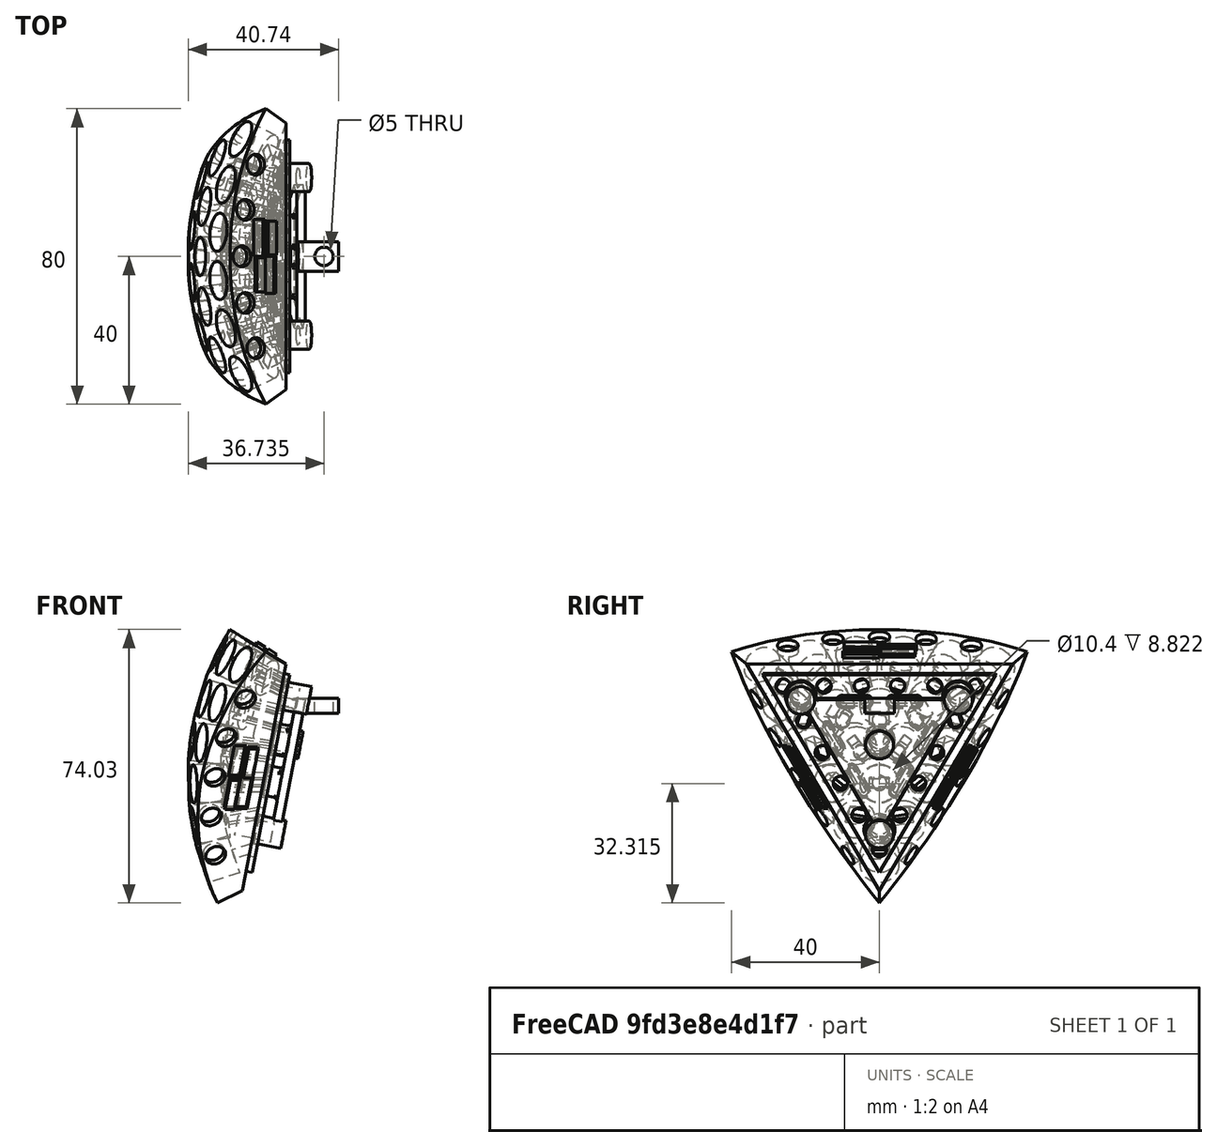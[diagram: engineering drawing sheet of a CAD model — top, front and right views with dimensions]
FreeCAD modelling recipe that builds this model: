
FCSTD DOCUMENT  (FreeCAD 0.20R27422 (Git))
Label: Inner_rev1
License: All rights reserved
LicenseURL: http://en.wikipedia.org/wiki/All_rights_reserved
objects: Part::Feature×3, Part::Part2DObjectPython×1, Part::Fillet×1, Part::Chamfer×1
note: 6 computed .brp shape members not serialized (recipe doc carries the construction recipe); baked Part::Feature solids carry a one-line shape summary decoded from their .brp

FEATURE [Part::Part2DObjectPython] Line  # Draft 2D object (typed FeaturePython)
  Area = 0
  ChamferSize = 0
  Closed = false
  End = (-60.4609,0,-2.48e-14)
  FilletRadius = 0
  Length = 60.4609
  MakeFace = true
  Points = (2) [(0,0,0),(-60.4609,0,-2.4803e-14)]
  Start = (0,0,0)
  Subdivisions = 0
FEATURE [Part::Feature] Shape
  Placement = pos=(0,0,0) rot=(0,1,0;0.188711rad)
  shape: bbox 26.49 x 83.96 x 75.99 mm, 229 faces (baked)
FEATURE [Part::Feature] Shape001
  Placement = pos=(0,0,0) rot=(0,1,0;0.188711rad)
  shape: bbox 11.8 x 62.95 x 53.85 mm, 64 faces (baked)
FEATURE [Part::Feature] Shape002
  shape: bbox 23.55 x 50.22 x 45.22 mm, 86 faces (baked)
FEATURE [Part::Fillet] Fillet
  Base = -> Shape002
  Edges = 6 edges r=1: [Edge30,Edge31,Edge36,Edge39,Edge44,Edge49]
FEATURE [Part::Chamfer] Chamfer
  Base = -> Fillet
  Edges = 10 edges r=0.7: [Edge49,Edge81,Edge126,Edge140,Edge162,Edge177,Edge180,Edge185,Edge202,Edge210]
